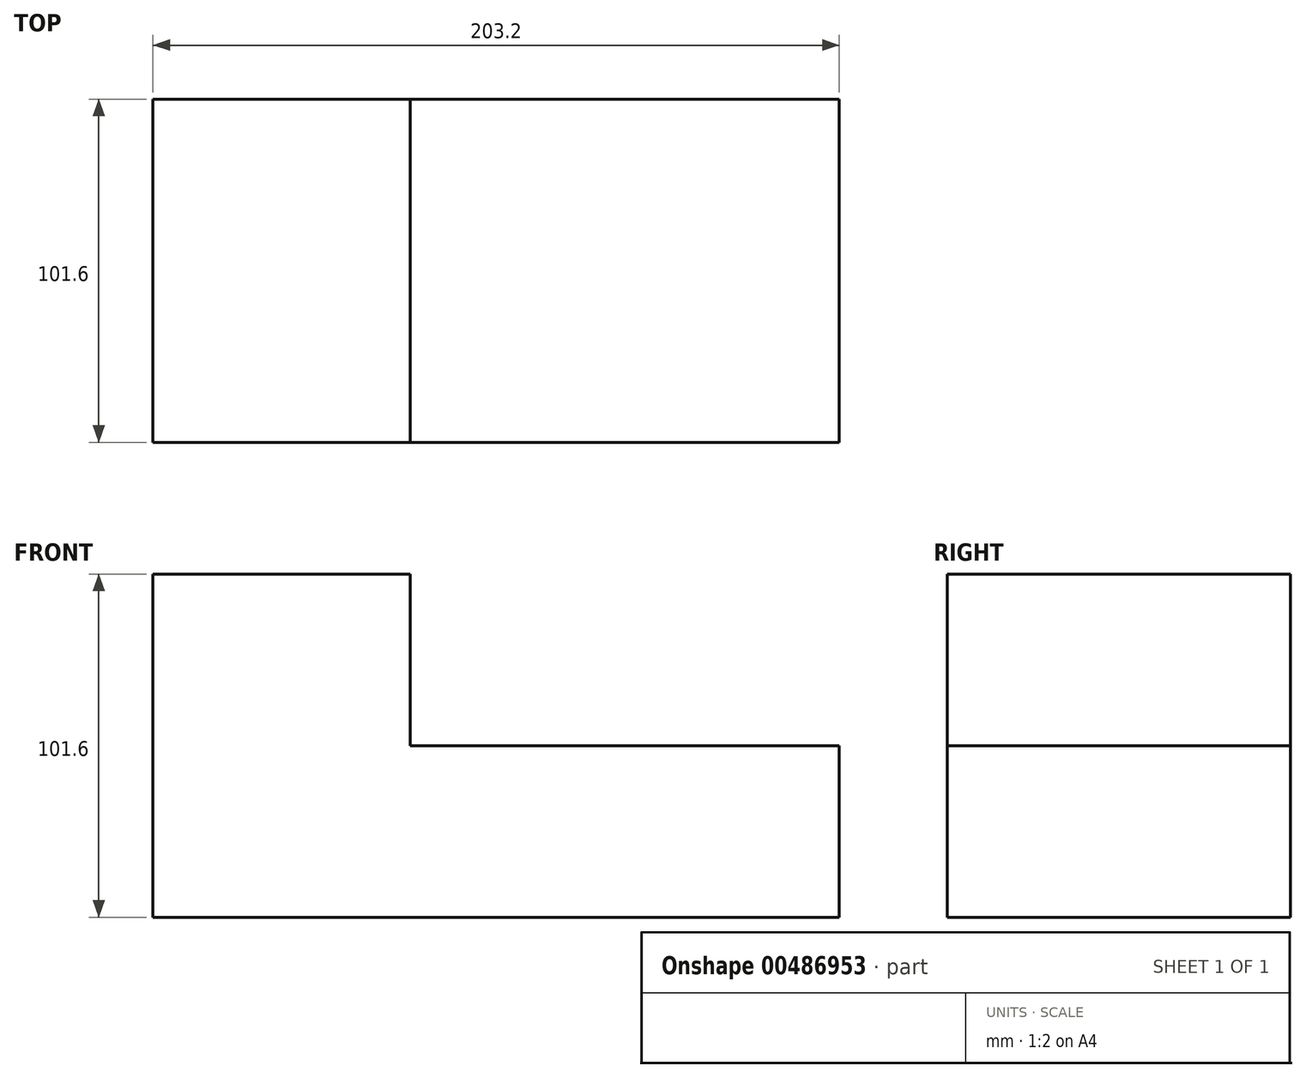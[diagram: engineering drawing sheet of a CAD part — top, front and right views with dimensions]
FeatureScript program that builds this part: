
annotation { "Feature Type Name" : "Feature", "Feature Type Description" : "" }
export const myFeature = defineFeature(function(context is Context, id is Id, definition is map)
    precondition{}
    {
        {
            var Q0;
            Q0=qCreatedBy(makeId("Front.planeOp"),FACE);
            var sketch = newSketch(context, id + "F0", { "sketchPlane" : qUnion([Q0])});
            skLineSegment(sketch, "E0.bottom", {"start": v(-87.36, 26.03) * mm, "end": v(39.64, 26.03) * mm});
            skLineSegment(sketch, "E0.top", {"start": v(-87.36, -24.77) * mm, "end": v(39.64, -24.77) * mm});
            skLineSegment(sketch, "E0.right", {"start": v(39.64, 26.03) * mm, "end": v(39.64, -24.77) * mm});
            skLineSegment(sketch, "E1.bottom", {"start": v(-87.36, -24.77) * mm, "end": v(-163.56, -24.77) * mm});
            skLineSegment(sketch, "E1.top", {"start": v(-87.36, 76.83) * mm, "end": v(-163.56, 76.83) * mm});
            skLineSegment(sketch, "E1.left", {"start": v(-87.36, 26.03) * mm, "end": v(-87.36, 76.83) * mm});
            skLineSegment(sketch, "E1.right", {"start": v(-163.56, -24.77) * mm, "end": v(-163.56, 76.83) * mm});
            skSolve(sketch);
        }
        {
            var Q0;
            Q0 = qSketchRegion(id + "F0", true);
            extrude(context, id + "F1", {"entities" : qUnion([Q0]), "depth" : 101.6 * mm});
        }
    });
